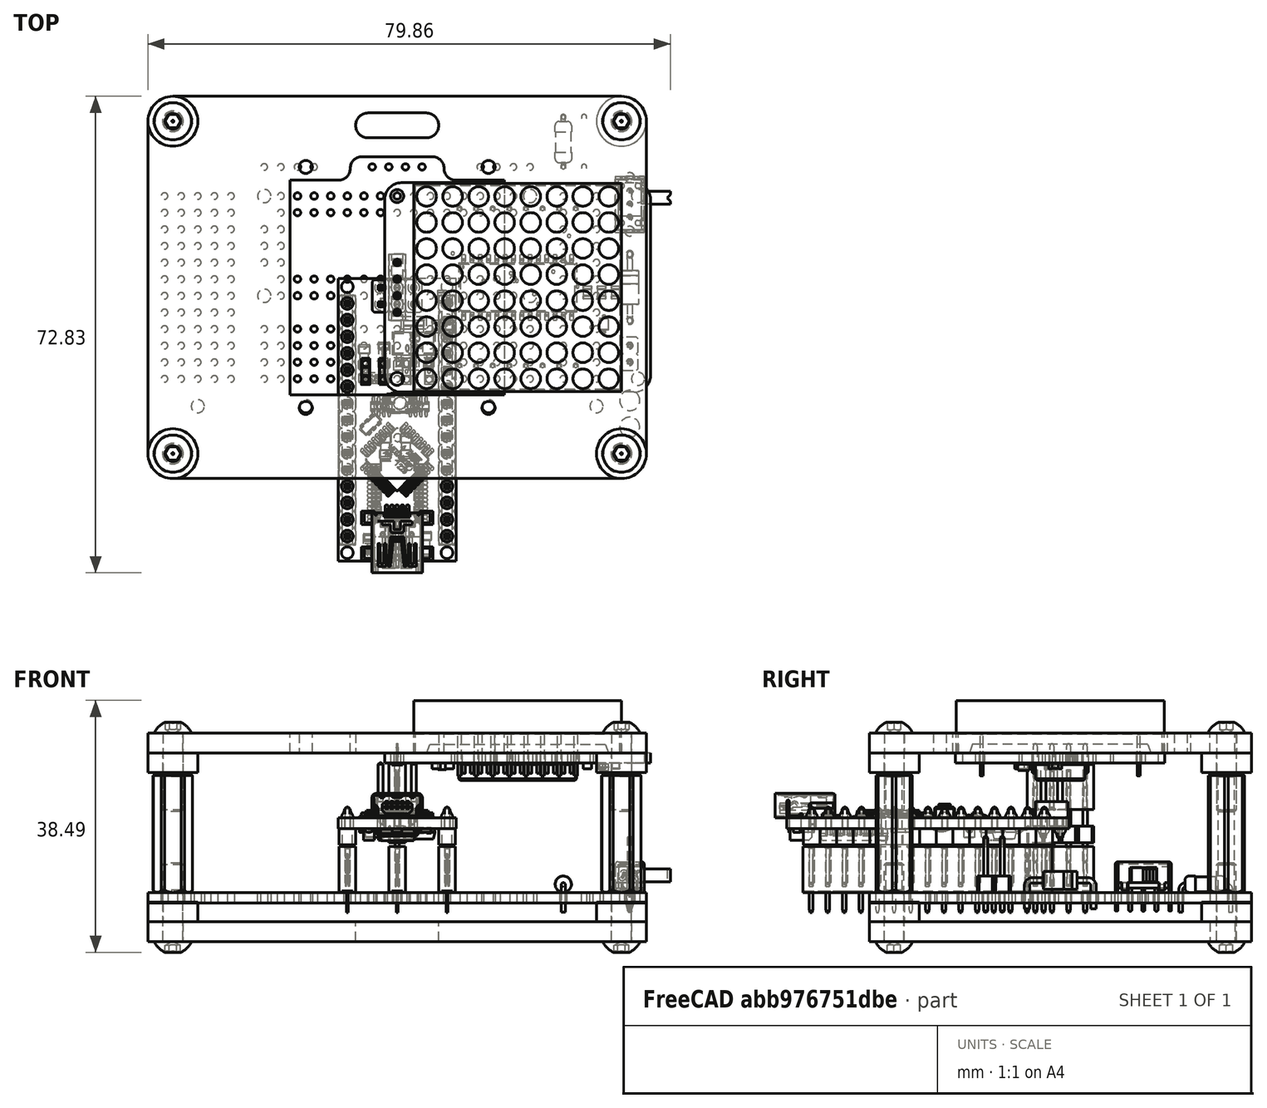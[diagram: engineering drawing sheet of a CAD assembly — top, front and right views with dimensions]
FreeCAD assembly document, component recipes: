
FREECAD ASSEMBLY — COMPONENT RECIPES ("BagTag_v2")

This assembly document has 5 components, labeled P0..P4 below (a component is one placed body or linked part). 4 of them carry a construction recipe — the FreeCAD feature program that regenerates the part from scratch, quoted from this document or its linked companion documents; the rest are supplied as boundary geometry only. No exploded tour is included for this assembly.
COMPONENT P0 — geometry summary ("BagTag"; no construction recipe available for this part):
  bounding box: 79.9 x 58.4 x 32.4 mm
  tessellated surface: 565,182 triangles
  volume: 33368 mm^3 (22% of its bounding box)
COMPONENT P1 — recipe-attached ("Plate_bottom", modeled in this document).
Construction recipe (the document's own serialized feature program — sketch geometry with constraints, then the solid features built on it; lengths are millimeters unless a unit is written):

FEATURE [PartDesign::SubShapeBinder] Binder  label="Binder(PCB_Sketch_fc76)"
  BindCopyOnChange = 0
  BindMode = 0
  ClaimChildren = false
  Context = -> Body [Binder.]
  Fuse = false
  MakeFace = true
  OffsetFill = false
  OffsetIntersection = false
  OffsetJoinType = 0
  OffsetOpenResult = false
  PartialLoad = false
  Relative = true
  Support = -> [Board_fc76[Board_Geoms_fc76.PCB_Sketch_fc76.]]
  _Version = 8
FEATURE [Sketcher::SketchObject] Sketch
  ExternalGeometry = -> [Binder]
  FullyConstrained = true
  MapMode = 5
  Support = -> [XY_Plane011]
  sketch-geometry (20):
    g0: LineSegment StartX=-34.29 StartY=29.21 StartZ=0 EndX=34.29 EndY=29.21 EndZ=0
    g1: LineSegment StartX=38.1 StartY=25.4 StartZ=0 EndX=38.1 EndY=-25.4 EndZ=0
    g2: LineSegment StartX=34.29 StartY=-29.21 StartZ=0 EndX=-34.29 EndY=-29.21 EndZ=0
    g3: LineSegment StartX=-38.1 StartY=-25.4 StartZ=0 EndX=-38.1 EndY=25.4 EndZ=0
    g4: ArcOfCircle CenterX=-34.29 CenterY=25.4 CenterZ=0 NormalX=0 NormalY=0 NormalZ=1 AngleXU=0 Radius=3.81 StartAngle=1.5708 EndAngle=3.14159
    g5: GeomPoint X=-38.1 Y=29.21 Z=0
    g6: ArcOfCircle CenterX=34.29 CenterY=25.4 CenterZ=0 NormalX=0 NormalY=0 NormalZ=1 AngleXU=0 Radius=3.81 StartAngle=0 EndAngle=1.5708
    g7: GeomPoint X=38.1 Y=29.21 Z=0
    g8: ArcOfCircle CenterX=34.29 CenterY=-25.4 CenterZ=0 NormalX=0 NormalY=0 NormalZ=1 AngleXU=0 Radius=3.81 StartAngle=4.71239 EndAngle=6.28319
    g9: GeomPoint X=38.1 Y=-29.21 Z=0
    g10: ArcOfCircle CenterX=-34.29 CenterY=-25.4 CenterZ=0 NormalX=0 NormalY=0 NormalZ=1 AngleXU=0 Radius=3.81 StartAngle=3.14159 EndAngle=4.71239
    g11: GeomPoint X=-38.1 Y=-29.21 Z=0
    g12: Circle CenterX=-34.29 CenterY=-25.4 CenterZ=0 NormalX=0 NormalY=0 NormalZ=1 AngleXU=0 Radius=1.524
    g13: Circle CenterX=34.29 CenterY=-25.4 CenterZ=0 NormalX=0 NormalY=0 NormalZ=1 AngleXU=0 Radius=1.524
    g14: Circle CenterX=34.29 CenterY=25.4 CenterZ=0 NormalX=0 NormalY=0 NormalZ=1 AngleXU=0 Radius=1.524
    g15: Circle CenterX=-34.29 CenterY=25.4 CenterZ=0 NormalX=0 NormalY=0 NormalZ=1 AngleXU=0 Radius=1.524
    g16: ArcOfCircle CenterX=-4.445 CenterY=24.765 CenterZ=0 NormalX=0 NormalY=0 NormalZ=1 AngleXU=0 Radius=1.905 StartAngle=1.5708 EndAngle=4.71239
    g17: ArcOfCircle CenterX=4.445 CenterY=24.765 CenterZ=0 NormalX=0 NormalY=0 NormalZ=1 AngleXU=0 Radius=1.905 StartAngle=4.71239 EndAngle=7.85398
    g18: LineSegment StartX=-4.445 StartY=22.86 StartZ=0 EndX=4.445 EndY=22.86 EndZ=0
    g19: LineSegment StartX=-4.445 StartY=26.67 StartZ=0 EndX=4.445 EndY=26.67 EndZ=0
  constraints (44):
    c: Horizontal(g0)
    c: Horizontal(g2)
    c: Vertical(g1)
    c: Vertical(g3)
    c: PointOnObject(g-4,g3)
    c: PointOnObject(g-5,g1)
    c: PointOnObject(g-3,g0)
    c: PointOnObject(g-6,g2)
    c: PointOnObject(g5,g0)
    c: PointOnObject(g5,g3)
    c: Tangent(g0,g4) = 1.5708
    c: Tangent(g3,g4) = 1.5708
    c: PointOnObject(g7,g0)
    c: PointOnObject(g7,g1)
    c: Tangent(g0,g6) = 1.5708
    c: Tangent(g1,g6) = 1.5708
    c: PointOnObject(g9,g1)
    c: PointOnObject(g9,g2)
    c: Tangent(g1,g8) = 1.5708
    c: Tangent(g2,g8) = 1.5708
    c: PointOnObject(g11,g3)
    c: PointOnObject(g11,g2)
    c: Tangent(g3,g10) = 1.5708
    c: Tangent(g2,g10) = 1.5708
    c: Equal(g10,g8)
    c: Equal(g8,g6)
    c: Equal(g6,g4)
    c: Equal(g4,g-14)
    c: Coincident(g12,g10)
    c: Coincident(g13,g8)
    c: Coincident(g14,g6)
    c: Coincident(g15,g4)
    c: Equal(g15,g14)
    c: Equal(g14,g13)
    c: Equal(g13,g12)
    c: Equal(g12,g-8)
    c: Tangent(g16,g19) = 1.5708
    c: Tangent(g16,g18) = -1.5708
    c: Tangent(g18,g17) = -1.5708
    c: Tangent(g19,g17) = 1.5708
    c: Horizontal(g18)
    c: Coincident(g16,g-13)
    c: PointOnObject(g17,g-12)
    c: Coincident(g17,g-12)
FEATURE [PartDesign::Pad] Pad
  Direction = (1,1,1)
  Length = 3
  Length2 = 100
  Profile = -> Sketch
  Reversed = true
  Type = 0
FEATURE [PartDesign::Body] Body  label="Plate_bottom"
  Group = -> [Sketch,Binder,Pad]
  Origin = -> Origin011
  Placement = pos=(0,0,-4.5) rot=(0,0,1;0rad)
  Tip = -> Pad
COMPONENT P2 — recipe-attached ("Spacers_bottom", modeled in this document).
Construction recipe (the document's own serialized feature program — sketch geometry with constraints, then the solid features built on it; lengths are millimeters unless a unit is written):

FEATURE [PartDesign::SubShapeBinder] Binder001  label="Binder001(Pad)"
  BindCopyOnChange = 0
  BindMode = 0
  ClaimChildren = false
  Context = -> Body001 [Binder001.]
  Fuse = false
  MakeFace = true
  OffsetFill = false
  OffsetIntersection = false
  OffsetJoinType = 0
  OffsetOpenResult = false
  PartialLoad = false
  Relative = true
  Support = -> [Body[Pad.]]
  _Version = 8
FEATURE [Sketcher::SketchObject] Sketch001
  ExternalGeometry = -> [Binder001]
  FullyConstrained = true
  MapMode = 5
  Placement = pos=(0,0,-4.5) rot=(0,0,1;0rad)
  Support = -> [Binder001]
  sketch-geometry (8):
    g0: Circle CenterX=-34.29 CenterY=25.4 CenterZ=0 NormalX=0 NormalY=0 NormalZ=1 AngleXU=0 Radius=1.524
    g1: Circle CenterX=34.29 CenterY=25.4 CenterZ=0 NormalX=0 NormalY=0 NormalZ=1 AngleXU=0 Radius=1.524
    g2: Circle CenterX=34.29 CenterY=-25.4 CenterZ=0 NormalX=0 NormalY=0 NormalZ=1 AngleXU=0 Radius=1.524
    g3: Circle CenterX=-34.29 CenterY=-25.4 CenterZ=0 NormalX=0 NormalY=0 NormalZ=1 AngleXU=0 Radius=1.524
    g4: Circle CenterX=-34.29 CenterY=-25.4 CenterZ=0 NormalX=0 NormalY=0 NormalZ=1 AngleXU=0 Radius=3.81
    g5: Circle CenterX=34.29 CenterY=-25.4 CenterZ=0 NormalX=0 NormalY=0 NormalZ=1 AngleXU=0 Radius=3.81
    g6: Circle CenterX=34.29 CenterY=25.4 CenterZ=0 NormalX=0 NormalY=0 NormalZ=1 AngleXU=0 Radius=3.81
    g7: Circle CenterX=-34.29 CenterY=25.4 CenterZ=0 NormalX=0 NormalY=0 NormalZ=1 AngleXU=0 Radius=3.81
  constraints (16):
    c: Coincident(g4,g3)
    c: Coincident(g5,g2)
    c: Coincident(g6,g1)
    c: Coincident(g7,g0)
    c: Equal(g0,g1)
    c: Equal(g1,g2)
    c: Equal(g2,g3)
    c: Equal(g4,g5)
    c: Equal(g5,g6)
    c: Equal(g6,g7)
    c: Coincident(g3,g-6)
    c: Coincident(g2,g-5)
    c: Coincident(g1,g-4)
    c: Coincident(g0,g-3)
    c: Equal(g3,g-6)
    c: Equal(g7,g-3)
FEATURE [PartDesign::Pad] Pad001
  Direction = (0,0,1)
  Length = 3
  Length2 = 100
  Profile = -> Sketch001
  Type = 0
FEATURE [PartDesign::Body] Body001  label="Spacers_bottom"
  Group = -> [Sketch001,Binder001,Pad001]
  Origin = -> Origin012
  Tip = -> Pad001
COMPONENT P3 — recipe-attached ("Plate_top", modeled in this document).
Construction recipe (the document's own serialized feature program — sketch geometry with constraints, then the solid features built on it; lengths are millimeters unless a unit is written):

FEATURE [PartDesign::SubShapeBinder] Binder002  label="Binder002(PCB_Sketch_fc76)"
  BindCopyOnChange = 0
  BindMode = 0
  ClaimChildren = false
  Context = -> Body002 [Binder002.]
  Fuse = false
  MakeFace = true
  OffsetFill = false
  OffsetIntersection = false
  OffsetJoinType = 0
  OffsetOpenResult = false
  PartialLoad = false
  Relative = true
  Support = -> [Board_fc76[Board_Geoms_fc76.PCB_Sketch_fc76.]]
  _Version = 8
FEATURE [PartDesign::SubShapeBinder] Binder003  label="Binder003(LED1_LED_matrix_8x8_socket004_4a1c2dfe1e64)"
  BindCopyOnChange = 0
  BindMode = 0
  ClaimChildren = false
  Context = -> Body002 [Binder003.]
  Fuse = false
  MakeFace = true
  OffsetFill = false
  OffsetIntersection = false
  OffsetJoinType = 0
  OffsetOpenResult = false
  PartialLoad = false
  Relative = true
  Support = -> [Board_fc76[Step_Models_fc76.Top_fc76.J2_LED_matrix_8x8_socket004_13e13e97bfa8_ln_001.]]
  _Version = 8
FEATURE [Sketcher::SketchObject] Sketch002
  ExternalGeometry = -> [Binder002,Binder003]
  FullyConstrained = true
  MapMode = 5
  Placement = pos=(2.6e-15,0,21.336) rot=(0,0,1;0rad)
  Support = -> [Binder003]
  sketch-geometry (41):
    g0: LineSegment StartX=-34.29 StartY=29.21 StartZ=0 EndX=34.29 EndY=29.21 EndZ=0
    g1: LineSegment StartX=38.1 StartY=25.4 StartZ=0 EndX=38.1 EndY=-25.4 EndZ=0
    g2: LineSegment StartX=34.29 StartY=-29.21 StartZ=0 EndX=-34.29 EndY=-29.21 EndZ=0
    g3: LineSegment StartX=-38.1 StartY=-25.4 StartZ=0 EndX=-38.1 EndY=25.4 EndZ=0
    g4: ArcOfCircle CenterX=-34.29 CenterY=25.4 CenterZ=0 NormalX=0 NormalY=0 NormalZ=1 AngleXU=0 Radius=3.81 StartAngle=1.5708 EndAngle=3.14159
    g5: GeomPoint X=-38.1 Y=29.21 Z=0
    g6: ArcOfCircle CenterX=34.29 CenterY=25.4 CenterZ=0 NormalX=0 NormalY=0 NormalZ=1 AngleXU=0 Radius=3.81 StartAngle=0 EndAngle=1.5708
    g7: GeomPoint X=38.1 Y=29.21 Z=0
    g8: ArcOfCircle CenterX=34.29 CenterY=-25.4 CenterZ=0 NormalX=0 NormalY=0 NormalZ=1 AngleXU=0 Radius=3.81 StartAngle=4.71239 EndAngle=6.28319
    g9: GeomPoint X=38.1 Y=-29.21 Z=0
    g10: ArcOfCircle CenterX=-34.29 CenterY=-25.4 CenterZ=0 NormalX=0 NormalY=0 NormalZ=1 AngleXU=0 Radius=3.81 StartAngle=3.14159 EndAngle=4.71239
    g11: GeomPoint X=-38.1 Y=-29.21 Z=0
    g12: Circle CenterX=-34.29 CenterY=-25.4 CenterZ=0 NormalX=0 NormalY=0 NormalZ=1 AngleXU=0 Radius=1.524
    g13: Circle CenterX=34.29 CenterY=-25.4 CenterZ=0 NormalX=0 NormalY=0 NormalZ=1 AngleXU=0 Radius=1.524
    g14: Circle CenterX=34.29 CenterY=25.4 CenterZ=0 NormalX=0 NormalY=0 NormalZ=1 AngleXU=0 Radius=1.524
    g15: Circle CenterX=-34.29 CenterY=25.4 CenterZ=0 NormalX=0 NormalY=0 NormalZ=1 AngleXU=0 Radius=1.524
    g16: ArcOfCircle CenterX=-4.445 CenterY=24.765 CenterZ=0 NormalX=0 NormalY=0 NormalZ=1 AngleXU=0 Radius=1.905 StartAngle=1.5708 EndAngle=4.71239
    g17: ArcOfCircle CenterX=4.44501 CenterY=24.765 CenterZ=0 NormalX=0 NormalY=0 NormalZ=1 AngleXU=0 Radius=1.905 StartAngle=4.71239 EndAngle=7.85398
    g18: LineSegment StartX=-4.445 StartY=22.86 StartZ=0 EndX=4.44501 EndY=22.86 EndZ=0
    g19: LineSegment StartX=-4.445 StartY=26.67 StartZ=0 EndX=4.44501 EndY=26.67 EndZ=0
    g20: LineSegment StartX=-16.4 StartY=16.4 StartZ=0 EndX=-8.965 EndY=16.4 EndZ=0
    g21: LineSegment StartX=16.4 StartY=16.4 StartZ=0 EndX=16.4 EndY=-16.4 EndZ=0
    g22: LineSegment StartX=16.4 StartY=-16.4 StartZ=0 EndX=-16.4 EndY=-16.4 EndZ=0
    g23: LineSegment StartX=-16.4 StartY=-16.4 StartZ=0 EndX=-16.4 EndY=16.4 EndZ=0
    g24: LineSegment StartX=-15.9 StartY=15.9 StartZ=0 EndX=-15.9 EndY=16.4 EndZ=0
    g25: LineSegment StartX=-15.9 StartY=15.9 StartZ=0 EndX=-16.4 EndY=15.9 EndZ=0
    g26: LineSegment StartX=15.9 StartY=-15.9 StartZ=0 EndX=16.4 EndY=-15.9 EndZ=0
    g27: LineSegment StartX=15.9 StartY=-15.9 StartZ=0 EndX=15.9 EndY=-16.4 EndZ=0
    g28: Circle CenterX=-13.97 CenterY=18.415 CenterZ=0 NormalX=0 NormalY=0 NormalZ=1 AngleXU=0 Radius=1
    g29: Circle CenterX=13.97 CenterY=18.415 CenterZ=0 NormalX=0 NormalY=0 NormalZ=1 AngleXU=0 Radius=1
    g30: Circle CenterX=13.97 CenterY=-18.415 CenterZ=0 NormalX=0 NormalY=0 NormalZ=1 AngleXU=0 Radius=1
    g31: Circle CenterX=-13.97 CenterY=-18.415 CenterZ=0 NormalX=0 NormalY=0 NormalZ=1 AngleXU=0 Radius=1
    g32: ArcOfCircle CenterX=-5.38 CenterY=18.1925 CenterZ=0 NormalX=0 NormalY=0 NormalZ=1 AngleXU=0 Radius=1.7925 StartAngle=1.5708 EndAngle=3.14159
    g33: ArcOfCircle CenterX=5.38 CenterY=18.1925 CenterZ=0 NormalX=0 NormalY=0 NormalZ=1 AngleXU=0 Radius=1.7925 StartAngle=4e-16 EndAngle=1.5708
    g34: LineSegment StartX=-5.38 StartY=19.985 StartZ=0 EndX=5.38 EndY=19.985 EndZ=0
    g35: LineSegment StartX=-5.08 StartY=19.685 StartZ=0 EndX=-5.08 EndY=19.985 EndZ=0
    g36: LineSegment StartX=-5.08 StartY=19.685 StartZ=0 EndX=-5.38 EndY=19.685 EndZ=0
    g37: LineSegment StartX=5.08 StartY=19.685 StartZ=0 EndX=5.38 EndY=19.685 EndZ=0
    g38: ArcOfCircle CenterX=-8.965 CenterY=18.1925 CenterZ=0 NormalX=0 NormalY=0 NormalZ=1 AngleXU=0 Radius=1.7925 StartAngle=4.71239 EndAngle=6.28319
    g39: ArcOfCircle CenterX=8.965 CenterY=18.1925 CenterZ=0 NormalX=0 NormalY=0 NormalZ=1 AngleXU=0 Radius=1.7925 StartAngle=3.14159 EndAngle=4.71239
    g40: LineSegment StartX=8.965 StartY=16.4 StartZ=0 EndX=16.4 EndY=16.4 EndZ=0
  constraints (101):
    c: Horizontal(g0)
    c: Horizontal(g2)
    c: Vertical(g1)
    c: Vertical(g3)
    c: PointOnObject(g-14,g3)
    c: PointOnObject(g-13,g1)
    c: PointOnObject(g-12,g2)
    c: PointOnObject(g-3,g0)
    c: PointOnObject(g5,g0)
    c: PointOnObject(g5,g3)
    c: Tangent(g0,g4) = 1.5708
    c: Tangent(g3,g4) = 1.5708
    c: PointOnObject(g7,g0)
    c: PointOnObject(g7,g1)
    c: Tangent(g0,g6) = 1.5708
    c: Tangent(g1,g6) = 1.5708
    c: PointOnObject(g9,g1)
    c: PointOnObject(g9,g2)
    c: Tangent(g1,g8) = 1.5708
    c: Tangent(g2,g8) = 1.5708
    c: PointOnObject(g11,g2)
    c: PointOnObject(g11,g3)
    c: Tangent(g2,g10) = 1.5708
    c: Tangent(g3,g10) = 1.5708
    c: Equal(g10,g8)
    c: Equal(g8,g6)
    c: Equal(g6,g4)
    c: Equal(g4,g-3)
    c: Coincident(g12,g10)
    c: Coincident(g13,g8)
    c: Coincident(g14,g6)
    c: Coincident(g15,g4)
    c: Equal(g-4,g15)
    c: Equal(g15,g14)
    c: Equal(g14,g13)
    c: Equal(g13,g12)
    c: Tangent(g16,g19) = 1.5708
    c: Tangent(g16,g18) = -1.5708
    c: Tangent(g18,g17) = -1.5708
    c: Tangent(g19,g17) = 1.5708
    c: Horizontal(g18)
    c: Equal(g16,g17)
    c: Coincident(g16,g-8)
    c: PointOnObject(g17,g-9)
    c: Equal(g16,g-8)
    c: Coincident(g40,g21)
    c: Coincident(g21,g22)
    c: Coincident(g22,g23)
    c: Coincident(g23,g20)
    c: Horizontal(g20)
    c: Horizontal(g22)
    c: Vertical(g21)
    c: Vertical(g23)
    c: Coincident(g24,g-10)
    c: PointOnObject(g24,g20)
    c: Vertical(g24)
    c: Coincident(g25,g-10)
    c: PointOnObject(g25,g23)
    c: Coincident(g26,g-11)
    c: PointOnObject(g26,g21)
    c: Horizontal(g26)
    c: Coincident(g27,g-11)
    c: PointOnObject(g27,g22)
    c: Vertical(g27)
    c: Horizontal(g25)
    c: Equal(g27,g26)
    c: Equal(g26,g24)
    c: Equal(g24,g25)
    c: DistanceY(g24,g24) = 0.5
    c: Coincident(g28,g-18)
    c: Tangent(g28,g-18)
    c: Coincident(g29,g-17)
    c: Tangent(g29,g-17)
    c: Coincident(g30,g-16)
    c: Tangent(g30,g-16)
    c: Coincident(g31,g-15)
    c: Equal(g-15,g31)
    c: Tangent(g32,g34) = 1.5708
    c: Tangent(g34,g33) = 1.5708
    c: Equal(g32,g33)
    c: Coincident(g35,g-19)
    c: PointOnObject(g35,g34)
    c: Vertical(g35)
    c: Coincident(g36,g-19)
    c: Horizontal(g36)
    c: Equal(g36,g35)
    c: Vertical(g36,g32)
    c: DistanceY(g35,g35) = 0.3
    c: Coincident(g37,g-19)
    c: Horizontal(g37)
    c: Equal(g37,g36)
    c: Vertical(g37,g33)
    c: Horizontal(g34)
    c: Tangent(g32,g38) = 1.5708
    c: Tangent(g33,g39) = 1.5708
    c: Equal(g38,g32)
    c: Equal(g32,g39)
    c: Horizontal(g38,g32)
    c: Tangent(g20,g38) = -1.5708
    c: Tangent(g40,g39) = -1.5708
    c: Tangent(g20,g40)
FEATURE [PartDesign::Pad] Pad002
  Direction = (1,1,1)
  Length = 3
  Length2 = 100
  Profile = -> Sketch002
  Type = 0
FEATURE [PartDesign::Body] Body002  label="Plate_top"
  Group = -> [Binder002,Binder003,Sketch002,Pad002]
  Origin = -> Origin013
  Tip = -> Pad002
COMPONENT P4 — recipe-attached ("Spacers_top", modeled in this document).
Construction recipe (the document's own serialized feature program — sketch geometry with constraints, then the solid features built on it; lengths are millimeters unless a unit is written):

FEATURE [PartDesign::SubShapeBinder] Binder004  label="Binder004(Pad002)"
  BindCopyOnChange = 0
  BindMode = 0
  ClaimChildren = false
  Context = -> Body003 [Binder004.]
  Fuse = false
  MakeFace = true
  OffsetFill = false
  OffsetIntersection = false
  OffsetJoinType = 0
  OffsetOpenResult = false
  PartialLoad = false
  Relative = true
  Support = -> [Body002[Pad002.Face31]]
  _Version = 8
FEATURE [Sketcher::SketchObject] Sketch003
  ExternalGeometry = -> [Binder004]
  FullyConstrained = true
  MapMode = 5
  Placement = pos=(2.3e-15,0,21.336) rot=(1,0,0;3.14159rad)
  Support = -> [Binder004]
  sketch-geometry (17):
    g0: Circle CenterX=-34.29 CenterY=25.4 CenterZ=0 NormalX=0 NormalY=0 NormalZ=1 AngleXU=0 Radius=1.524
    g1: Circle CenterX=34.29 CenterY=25.4 CenterZ=0 NormalX=0 NormalY=0 NormalZ=1 AngleXU=0 Radius=1.524
    g2: Circle CenterX=34.29 CenterY=-25.4 CenterZ=0 NormalX=0 NormalY=0 NormalZ=1 AngleXU=0 Radius=1.524
    g3: Circle CenterX=-34.29 CenterY=-25.4 CenterZ=0 NormalX=0 NormalY=0 NormalZ=1 AngleXU=0 Radius=1.524
    g4: Circle CenterX=-34.29 CenterY=25.4 CenterZ=0 NormalX=0 NormalY=0 NormalZ=1 AngleXU=0 Radius=3.81
    g5: Circle CenterX=34.29 CenterY=25.4 CenterZ=0 NormalX=0 NormalY=0 NormalZ=1 AngleXU=0 Radius=3.81
    g6: Circle CenterX=34.29 CenterY=-25.4 CenterZ=0 NormalX=0 NormalY=0 NormalZ=1 AngleXU=0 Radius=3.81
    g7: Circle CenterX=-34.29 CenterY=-25.4 CenterZ=0 NormalX=0 NormalY=0 NormalZ=1 AngleXU=0 Radius=3.81
    g8: Circle CenterX=-10 CenterY=10 CenterZ=0 NormalX=0 NormalY=0 NormalZ=1 AngleXU=0 Radius=3.81
    g9: Circle CenterX=0 CenterY=10 CenterZ=0 NormalX=0 NormalY=0 NormalZ=1 AngleXU=0 Radius=3.81
    g10: Circle CenterX=10 CenterY=10 CenterZ=0 NormalX=0 NormalY=0 NormalZ=1 AngleXU=0 Radius=3.81
    g11: Circle CenterX=-10 CenterY=0 CenterZ=0 NormalX=0 NormalY=0 NormalZ=1 AngleXU=0 Radius=3.81
    g12: Circle CenterX=0 CenterY=0 CenterZ=0 NormalX=0 NormalY=0 NormalZ=1 AngleXU=0 Radius=3.81
    g13: Circle CenterX=10 CenterY=0 CenterZ=0 NormalX=0 NormalY=0 NormalZ=1 AngleXU=0 Radius=3.81
    g14: Circle CenterX=-10 CenterY=-10 CenterZ=0 NormalX=0 NormalY=0 NormalZ=1 AngleXU=0 Radius=3.81
    g15: Circle CenterX=0 CenterY=-10 CenterZ=0 NormalX=0 NormalY=0 NormalZ=1 AngleXU=0 Radius=3.81
    g16: Circle CenterX=10 CenterY=-10 CenterZ=0 NormalX=0 NormalY=0 NormalZ=1 AngleXU=0 Radius=3.81
  constraints (40):
    c: Coincident(g0,g-3)
    c: Equal(g0,g1)
    c: Equal(g1,g2)
    c: Equal(g2,g3)
    c: Equal(g3,g-4)
    c: Coincident(g1,g-4)
    c: Coincident(g2,g-5)
    c: Coincident(g3,g-6)
    c: Coincident(g4,g0)
    c: Coincident(g5,g1)
    c: Coincident(g6,g2)
    c: Coincident(g7,g3)
    c: Equal(g7,g6)
    c: Equal(g6,g5)
    c: Equal(g5,g4)
    c: Equal(g4,g-3)
    c: Equal(g16,g15)
    c: Equal(g15,g14)
    c: Equal(g14,g11)
    c: Equal(g11,g12)
    c: Equal(g12,g13)
    c: Equal(g13,g10)
    c: Equal(g10,g9)
    c: Equal(g9,g8)
    c: Equal(g8,g4)
    c: Horizontal(g8,g9)
    c: Horizontal(g9,g10)
    c: Horizontal(g11,g12)
    c: Horizontal(g14,g15)
    c: Horizontal(g15,g16)
    c: Vertical(g14,g11)
    c: Vertical(g11,g8)
    c: Vertical(g15,g12)
    c: Vertical(g16,g13)
    c: Vertical(g13,g10)
    c: Coincident(g12,g-1)
    c: Symmetric(g11,g13,g-2)
    c: Symmetric(g9,g15,g-1)
    c: DistanceX(g8,g9) = 10
    c: DistanceY(g11,g8) = 10
FEATURE [PartDesign::Pad] Pad003
  Direction = (1,1,1)
  Length = 3
  Length2 = 100
  Profile = -> Sketch003
  Type = 0
FEATURE [PartDesign::Body] Body003  label="Spacers_top"
  Group = -> [Binder004,Sketch003,Pad003]
  Origin = -> Origin014
  Tip = -> Pad003
PROVENANCE & LICENSES
A FreeCAD (.FCStd) document from a public repository crawl; recipes are the document's own serialized feature recipes (and, for linked parts, companion documents' recipes).
License: gpl-3.0.
